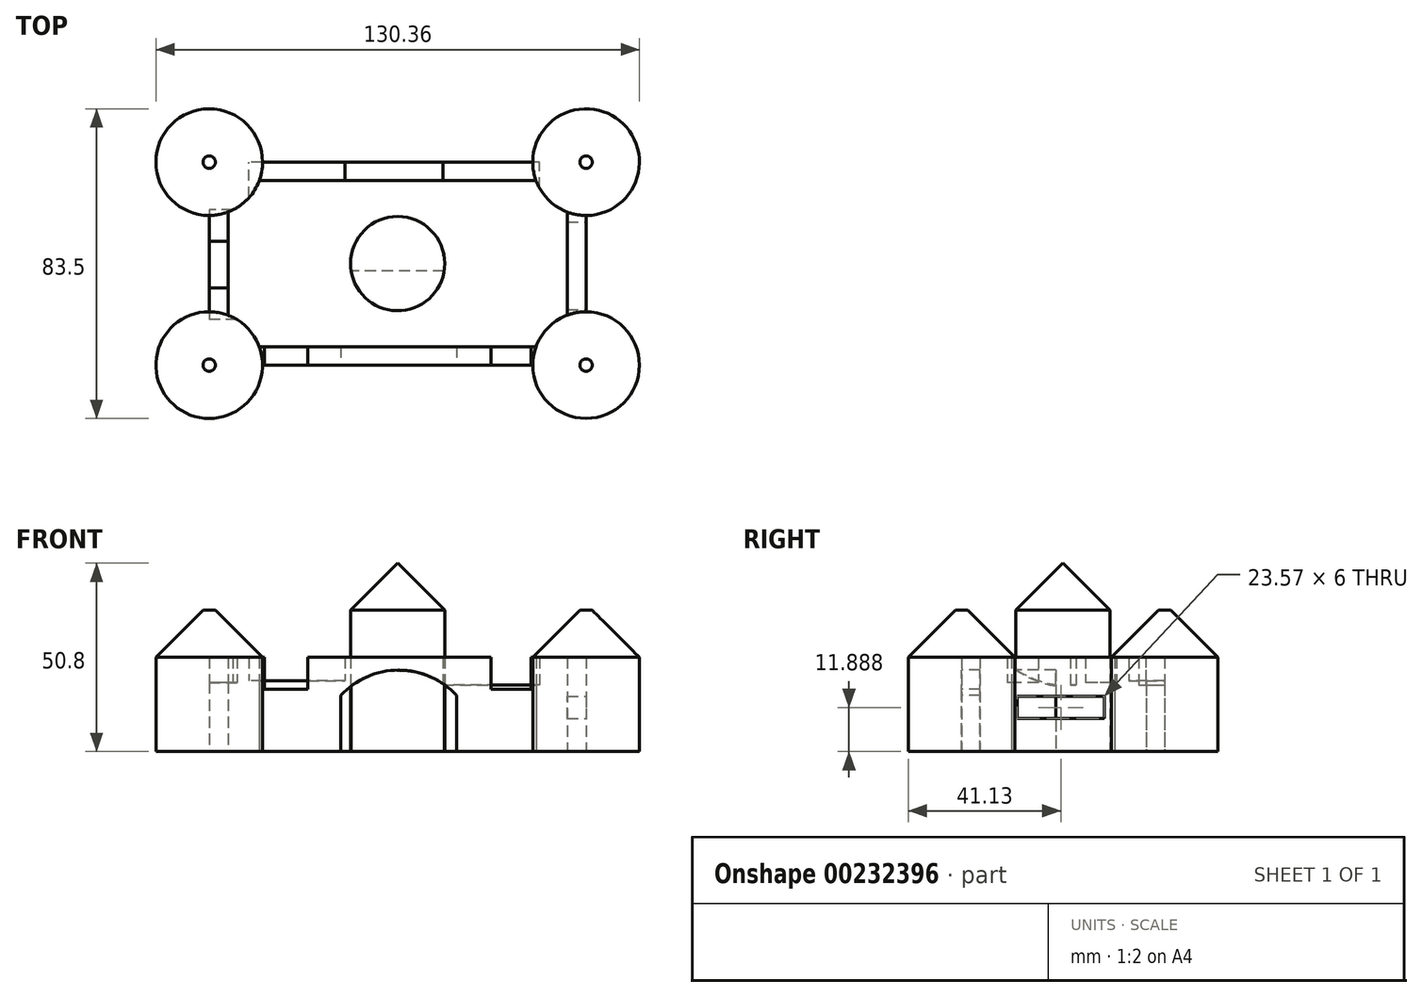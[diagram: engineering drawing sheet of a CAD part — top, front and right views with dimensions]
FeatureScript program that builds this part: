
annotation { "Feature Type Name" : "Feature", "Feature Type Description" : "" }
export const myFeature = defineFeature(function(context is Context, id is Id, definition is map)
    precondition{}
    {
        {
            var Q0;
            Q0=qCreatedBy(makeId("Top.planeOp"),FACE);
            var sketch = newSketch(context, id + "F0", { "sketchPlane" : qUnion([Q0])});
            skLineSegment(sketch, "E0.bottom", {"start": v(36.42, 27.36) * mm, "end": v(-36.42, 27.36) * mm});
            skLineSegment(sketch, "E0.top", {"start": v(36.42, -27.36) * mm, "end": v(-36.42, -27.36) * mm});
            skLineSegment(sketch, "E0.left", {"start": v(50.8, 12.98) * mm, "end": v(50.8, -12.98) * mm});
            skLineSegment(sketch, "E0.right", {"start": v(-50.8, 12.98) * mm, "end": v(-50.8, -12.98) * mm});
            skPoint(sketch, "E0.middle", {"position": v(0, 0) * mm});
            skCircle(sketch, "E1", {"center": v(0, 0) * mm, "radius": 12.7 * mm});
            skCircle(sketch, "E2", {"center": v(50.8, -27.36) * mm, "radius": 14.38 * mm});
            skCircle(sketch, "E3", {"center": v(50.8, 27.36) * mm, "radius": 14.38 * mm});
            skCircle(sketch, "E4", {"center": v(-50.8, -27.36) * mm, "radius": 14.38 * mm});
            skCircle(sketch, "E5", {"center": v(-50.8, 27.36) * mm, "radius": 14.38 * mm});
            skLineSegment(sketch, "E6.bottom", {"start": v(37.3, -22.38) * mm, "end": v(-37.3, -22.38) * mm});
            skLineSegment(sketch, "E6.top", {"start": v(37.3, 22.38) * mm, "end": v(-37.3, 22.38) * mm});
            skLineSegment(sketch, "E6.left", {"start": v(45.72, -13.9) * mm, "end": v(45.72, 13.9) * mm});
            skLineSegment(sketch, "E6.right", {"start": v(-45.72, -13.9) * mm, "end": v(-45.72, 13.9) * mm});
            skPoint(sketch, "E7.orphan", {"position": v(45.72, 22.38) * mm});
            skPoint(sketch, "E8.orphan", {"position": v(-45.72, 22.38) * mm});
            skPoint(sketch, "E9.orphan", {"position": v(45.72, -22.38) * mm});
            skPoint(sketch, "E10.orphan", {"position": v(-45.72, -22.38) * mm});
            skSolve(sketch);
        }
        {
            var Q0;
            {var subQ0=sQuery(id+"F0.wireOp",EDGE,"E0.bottom");Q0=makeQuery(id+"F0.imprint","IMPRINT",FACE,{"disambiguationData":[TD([[makeQuery(id+"F0.imprint","IMPRINT",EDGE,{"derivedFrom":subQ0}),1.0]])]});}
            var Q1;
            {var subQ0=sQuery(id+"F0.wireOp",EDGE,"E0.right");Q1=makeQuery(id+"F0.imprint","IMPRINT",FACE,{"disambiguationData":[TD([[makeQuery(id+"F0.imprint","IMPRINT",EDGE,{"derivedFrom":subQ0}),1.0]])]});}
            var Q2;
            {var subQ0=sQuery(id+"F0.wireOp",EDGE,"E0.left");Q2=makeQuery(id+"F0.imprint","IMPRINT",FACE,{"disambiguationData":[TD([[makeQuery(id+"F0.imprint","IMPRINT",EDGE,{"derivedFrom":subQ0}),-1.0]])]});}
            var Q3;
            {var subQ0=sQuery(id+"F0.wireOp",EDGE,"E0.top");Q3=makeQuery(id+"F0.imprint","IMPRINT",FACE,{"disambiguationData":[TD([[makeQuery(id+"F0.imprint","IMPRINT",EDGE,{"derivedFrom":subQ0}),-1.0]])]});}
            extrude(context, id + "F1", {"entities" : qUnion([Q0, Q1, Q2, Q3]), "depth" : 25.4 * mm});
        }
        {
            var Q0;
            {var subQ0=sQuery(id+"F0.wireOp",EDGE,"E5");var subQ1=makeQuery(id+"F0.imprint","INTERSECT",VERTEX,{"derivedFrom":[sQuery(id+"F0.wireOp",EDGE,"E0.bottom"),subQ0]});Q0=makeQuery(id+"F0.imprint","IMPRINT",FACE,{"disambiguationData":[TD([[makeQuery(id+"F0.imprint","IMPRINT",EDGE,{"disambiguationData":[TD([[subQ1,-1.0]])],"derivedFrom":subQ0}),1.0]])]});}
            var Q1;
            {var subQ0=sQuery(id+"F0.wireOp",EDGE,"E3");var subQ1=makeQuery(id+"F0.imprint","INTERSECT",VERTEX,{"derivedFrom":[sQuery(id+"F0.wireOp",EDGE,"E0.bottom"),subQ0]});Q1=makeQuery(id+"F0.imprint","IMPRINT",FACE,{"disambiguationData":[TD([[makeQuery(id+"F0.imprint","IMPRINT",EDGE,{"disambiguationData":[TD([[subQ1,-1.0]])],"derivedFrom":subQ0}),1.0]])]});}
            var Q2;
            {var subQ0=sQuery(id+"F0.wireOp",EDGE,"E2");var subQ1=makeQuery(id+"F0.imprint","INTERSECT",VERTEX,{"derivedFrom":[sQuery(id+"F0.wireOp",EDGE,"E0.left"),subQ0]});Q2=makeQuery(id+"F0.imprint","IMPRINT",FACE,{"disambiguationData":[TD([[makeQuery(id+"F0.imprint","IMPRINT",EDGE,{"disambiguationData":[TD([[subQ1,-1.0]])],"derivedFrom":subQ0}),1.0]])]});}
            var Q3;
            {var subQ0=sQuery(id+"F0.wireOp",EDGE,"E4");var subQ1=makeQuery(id+"F0.imprint","INTERSECT",VERTEX,{"derivedFrom":[sQuery(id+"F0.wireOp",EDGE,"E0.top"),subQ0]});Q3=makeQuery(id+"F0.imprint","IMPRINT",FACE,{"disambiguationData":[TD([[makeQuery(id+"F0.imprint","IMPRINT",EDGE,{"disambiguationData":[TD([[subQ1,-1.0]])],"derivedFrom":subQ0}),1.0]])]});}
            extrude(context, id + "F2", {"entities" : qUnion([Q0, Q1, Q2, Q3]), "depth" : 38.1 * mm});
        }
        {
            var Q0;
            Q0=makeQuery(id+"F0.imprint","IMPRINT",FACE,{"disambiguationData":[TD([[makeQuery(id+"F0.imprint","IMPRINT",EDGE,{"derivedFrom":sQuery(id+"F0.wireOp",EDGE,"E1")}),1.0]])]});
            extrude(context, id + "F3", {"entities" : qUnion([Q0]), "depth" : 50.8 * mm});
        }
        {
            var Q0;
            Q0=makeQuery(id+"F1.opExtrude","SWEPT_FACE",FACE,{"disambiguationData":[OSD([sQuery(id+"F0.wireOp",EDGE,"E0.top")])]});
            var sketch = newSketch(context, id + "F4", { "sketchPlane" : qUnion([Q0])});
            skLineSegment(sketch, "E11.bottom", {"start": v(-15.3, 0) * mm, "end": v(15.92, 0) * mm});
            skLineSegment(sketch, "E11.left", {"start": v(-15.3, 0) * mm, "end": v(-15.3, 15.1) * mm});
            skLineSegment(sketch, "E11.right", {"start": v(15.92, 0) * mm, "end": v(15.92, 15.1) * mm});
            skArc(sketch, "E12", {"start": v(15.92, 15.1) * mm, "mid": v(0.31, 21.93) * mm, "end": v(-15.3, 15.1) * mm});
            skLineSegment(sketch, "E13.bottom", {"start": v(-35.97, 25.64) * mm, "end": v(-24.19, 25.64) * mm});
            skLineSegment(sketch, "E13.top", {"start": v(-35.97, 16.75) * mm, "end": v(-24.19, 16.75) * mm});
            skLineSegment(sketch, "E13.left", {"start": v(-35.97, 25.64) * mm, "end": v(-35.97, 16.75) * mm});
            skLineSegment(sketch, "E13.right", {"start": v(-24.19, 25.64) * mm, "end": v(-24.19, 16.75) * mm});
            skLineSegment(sketch, "E14.top", {"start": v(25.22, 25.64) * mm, "end": v(35.35, 25.64) * mm});
            skLineSegment(sketch, "E15.bottom", {"start": v(25.22, 25.64) * mm, "end": v(35.97, 25.64) * mm});
            skLineSegment(sketch, "E15.top", {"start": v(25.22, 16.75) * mm, "end": v(35.97, 16.75) * mm});
            skLineSegment(sketch, "E15.left", {"start": v(25.22, 25.64) * mm, "end": v(25.22, 16.75) * mm});
            skLineSegment(sketch, "E15.right", {"start": v(35.97, 25.64) * mm, "end": v(35.97, 16.75) * mm});
            skSolve(sketch);
        }
        {
            var Q0;
            Q0=makeQuery(id+"F4.imprint","IMPRINT",FACE,{"disambiguationData":[TD([[makeQuery(id+"F4.imprint","IMPRINT",EDGE,{"derivedFrom":sQuery(id+"F4.wireOp",EDGE,"E11.bottom")}),-1.0]])]});
            extrude(context, id + "F5", {"entities" : qUnion([Q0]), "operationType" : NewBodyOperationType.REMOVE, "oppositeDirection" : true, "depth" : 25.4 * mm});
        }
        {
            var Q0;
            {var subQ0=sQuery(id+"F4.wireOp",EDGE,"E13.top");Q0=makeQuery(id+"F4.imprint","IMPRINT",FACE,{"disambiguationData":[TD([[makeQuery(id+"F4.imprint","IMPRINT",EDGE,{"derivedFrom":subQ0}),1.0]])]});}
            var Q1;
            {var subQ0=sQuery(id+"F4.wireOp",EDGE,"E15.top");Q1=makeQuery(id+"F4.imprint","IMPRINT",FACE,{"disambiguationData":[TD([[makeQuery(id+"F4.imprint","IMPRINT",EDGE,{"derivedFrom":subQ0}),1.0]])]});}
            extrude(context, id + "F6", {"entities" : qUnion([Q0, Q1]), "operationType" : NewBodyOperationType.REMOVE, "oppositeDirection" : true, "depth" : 25.4 * mm});
        }
        {
            var Q0;
            Q0=makeQuery(id+"F1.opExtrude","SWEPT_FACE",FACE,{"disambiguationData":[OSD([sQuery(id+"F0.wireOp",EDGE,"E0.right")])]});
            var sketch = newSketch(context, id + "F7", { "sketchPlane" : qUnion([Q0])});
            skLineSegment(sketch, "E16.bottom", {"start": v(-14.47, 25.4) * mm, "end": v(-6, 25.4) * mm});
            skLineSegment(sketch, "E16.top", {"start": v(-14.47, 18.6) * mm, "end": v(-6, 18.6) * mm});
            skLineSegment(sketch, "E16.left", {"start": v(-14.47, 25.4) * mm, "end": v(-14.47, 18.6) * mm});
            skLineSegment(sketch, "E16.right", {"start": v(-6, 25.4) * mm, "end": v(-6, 18.6) * mm});
            skLineSegment(sketch, "E17.bottom", {"start": v(6.62, 25.4) * mm, "end": v(15.1, 25.4) * mm});
            skLineSegment(sketch, "E17.top", {"start": v(6.62, 18.6) * mm, "end": v(15.1, 18.6) * mm});
            skLineSegment(sketch, "E17.left", {"start": v(6.62, 25.4) * mm, "end": v(6.62, 18.6) * mm});
            skLineSegment(sketch, "E17.right", {"start": v(15.1, 25.4) * mm, "end": v(15.1, 18.6) * mm});
            skSolve(sketch);
        }
        {
            var Q0;
            Q0=makeQuery(id+"F7.imprint","IMPRINT",FACE,{"disambiguationData":[TD([[makeQuery(id+"F7.imprint","IMPRINT",EDGE,{"derivedFrom":sQuery(id+"F7.wireOp",EDGE,"E16.bottom")}),-1.0]])]});
            var Q1;
            Q1=makeQuery(id+"F7.imprint","IMPRINT",FACE,{"disambiguationData":[TD([[makeQuery(id+"F7.imprint","IMPRINT",EDGE,{"derivedFrom":sQuery(id+"F7.wireOp",EDGE,"E17.bottom")}),-1.0]])]});
            extrude(context, id + "F8", {"entities" : qUnion([Q0, Q1]), "operationType" : NewBodyOperationType.REMOVE, "oppositeDirection" : true, "depth" : 25.4 * mm});
        }
        {
            var Q0;
            Q0=makeQuery(id+"F1.opExtrude","SWEPT_FACE",FACE,{"disambiguationData":[OSD([sQuery(id+"F0.wireOp",EDGE,"E0.left")])]});
            var sketch = newSketch(context, id + "F9", { "sketchPlane" : qUnion([Q0])});
            skLineSegment(sketch, "E18.bottom", {"start": v(-12.4, 14.89) * mm, "end": v(11.16, 14.89) * mm});
            skLineSegment(sketch, "E18.top", {"start": v(-12.4, 8.9) * mm, "end": v(11.16, 8.9) * mm});
            skLineSegment(sketch, "E18.left", {"start": v(-12.4, 14.89) * mm, "end": v(-12.4, 8.9) * mm});
            skLineSegment(sketch, "E18.right", {"start": v(11.16, 14.89) * mm, "end": v(11.16, 8.9) * mm});
            skSolve(sketch);
        }
        {
            var Q0;
            Q0=makeQuery(id+"F9.imprint","IMPRINT",FACE,{"disambiguationData":[TD([[makeQuery(id+"F9.imprint","IMPRINT",EDGE,{"derivedFrom":sQuery(id+"F9.wireOp",EDGE,"E18.bottom")}),-1.0]])]});
            extrude(context, id + "F10", {"entities" : qUnion([Q0]), "operationType" : NewBodyOperationType.REMOVE, "oppositeDirection" : true, "depth" : 25.4 * mm});
        }
        {
            var Q0;
            Q0=makeQuery(id+"F1.opExtrude","SWEPT_FACE",FACE,{"disambiguationData":[OSD([sQuery(id+"F0.wireOp",EDGE,"E0.bottom")])]});
            var sketch = newSketch(context, id + "F11", { "sketchPlane" : qUnion([Q0])});
            skLineSegment(sketch, "E19.bottom", {"start": v(-38.25, 25.4) * mm, "end": v(-12.2, 25.4) * mm});
            skLineSegment(sketch, "E19.top", {"start": v(-38.25, 17.99) * mm, "end": v(-12.2, 17.99) * mm});
            skLineSegment(sketch, "E19.left", {"start": v(-38.25, 25.4) * mm, "end": v(-38.25, 17.99) * mm});
            skLineSegment(sketch, "E19.right", {"start": v(-12.2, 25.4) * mm, "end": v(-12.2, 17.99) * mm});
            skLineSegment(sketch, "E20.bottom", {"start": v(14.27, 25.4) * mm, "end": v(40.1, 25.4) * mm});
            skLineSegment(sketch, "E20.top", {"start": v(14.27, 19.02) * mm, "end": v(40.1, 19.02) * mm});
            skLineSegment(sketch, "E20.left", {"start": v(14.27, 25.4) * mm, "end": v(14.27, 19.02) * mm});
            skLineSegment(sketch, "E20.right", {"start": v(40.1, 25.4) * mm, "end": v(40.1, 19.02) * mm});
            skSolve(sketch);
        }
        {
            var Q0;
            Q0=makeQuery(id+"F11.imprint","IMPRINT",FACE,{"disambiguationData":[TD([[makeQuery(id+"F11.imprint","IMPRINT",EDGE,{"derivedFrom":sQuery(id+"F11.wireOp",EDGE,"E19.bottom")}),-1.0]])]});
            var Q1;
            Q1=makeQuery(id+"F11.imprint","IMPRINT",FACE,{"disambiguationData":[TD([[makeQuery(id+"F11.imprint","IMPRINT",EDGE,{"derivedFrom":sQuery(id+"F11.wireOp",EDGE,"E20.bottom")}),-1.0]])]});
            extrude(context, id + "F12", {"entities" : qUnion([Q0, Q1]), "operationType" : NewBodyOperationType.REMOVE, "oppositeDirection" : true, "depth" : 25.4 * mm});
        }
        {
            var Q0;
            Q0=makeQuery(id+"F3.opExtrude","CAP_FACE",FACE,{"disambiguationData":[OSD([sQuery(id+"F0.wireOp",EDGE,"E1")])],"isStart":false});
            chamfer(context, id + "F13", {"entities" : qUnion([Q0]), "width" : 12.7 * mm, "tangentPropagation" : true});
        }
        {
            var Q0;
            Q0=makeQuery(id+"F2.opExtrude","CAP_FACE",FACE,{"disambiguationData":[OSD([sQuery(id+"F0.wireOp",EDGE,"E5")])],"isStart":false});
            var Q1;
            Q1=makeQuery(id+"F2.opExtrude","CAP_FACE",FACE,{"disambiguationData":[OSD([sQuery(id+"F0.wireOp",EDGE,"E2")])],"isStart":false});
            var Q2;
            Q2=makeQuery(id+"F2.opExtrude","CAP_FACE",FACE,{"disambiguationData":[OSD([sQuery(id+"F0.wireOp",EDGE,"E3")])],"isStart":false});
            var Q3;
            Q3=makeQuery(id+"F2.opExtrude","CAP_FACE",FACE,{"disambiguationData":[OSD([sQuery(id+"F0.wireOp",EDGE,"E4")])],"isStart":false});
            chamfer(context, id + "F14", {"entities" : qUnion([Q0, Q1, Q2, Q3]), "width" : 12.7 * mm, "tangentPropagation" : true});
        }
    });
